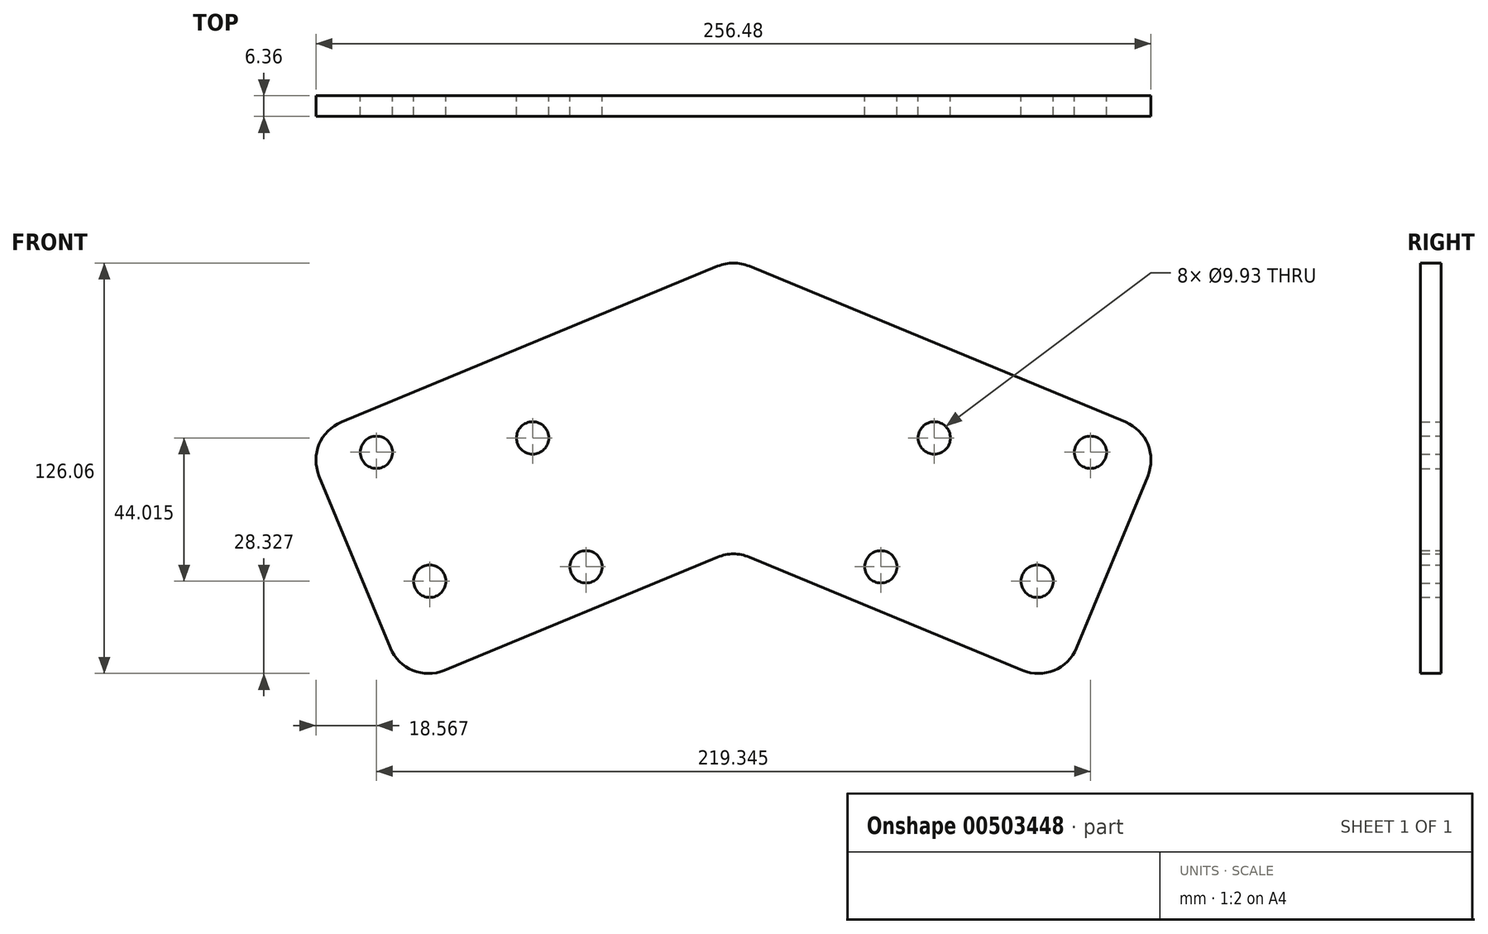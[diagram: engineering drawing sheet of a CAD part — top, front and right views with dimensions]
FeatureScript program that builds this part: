
annotation { "Feature Type Name" : "Feature", "Feature Type Description" : "" }
export const myFeature = defineFeature(function(context is Context, id is Id, definition is map)
    precondition{}
    {
        {
            var Q0;
            Q0=qCreatedBy(makeId("Front.planeOp"),FACE);
            var sketch = newSketch(context, id + "F0", { "sketchPlane" : qUnion([Q0])});
            skLineSegment(sketch, "E0", {"start": v(0, 0) * mm, "end": v(-100.54, -41.65) * mm});
            skLineSegment(sketch, "E1", {"start": v(0, 0) * mm, "end": v(0, 89.35) * mm});
            skLineSegment(sketch, "E2", {"start": v(-100.54, -41.65) * mm, "end": v(-132.13, 34.62) * mm});
            skLineSegment(sketch, "E3", {"start": v(-132.13, 34.62) * mm, "end": v(0, 89.35) * mm});
            skPoint(sketch, "E4", {"position": v(-15.88, 98.24) * mm});
            skPoint(sketch, "E5", {"position": v(-15.88, -22.04) * mm});
            skLineSegment(sketch, "E6.MirrorCS", {"start": v(0, 0) * mm, "end": v(100.54, -41.65) * mm});
            skPoint(sketch, "E7.MirrorP", {"position": v(15.88, -22.04) * mm});
            skLineSegment(sketch, "E8.MirrorCS", {"start": v(100.54, -41.65) * mm, "end": v(132.13, 34.62) * mm});
            skLineSegment(sketch, "E9.MirrorCS", {"start": v(132.13, 34.62) * mm, "end": v(0, 89.35) * mm});
            skPoint(sketch, "E10.MirrorP", {"position": v(15.88, 98.24) * mm});
            skLineSegment(sketch, "E11", {"start": v(-15.88, -22.04) * mm, "end": v(-45.04, 48.36) * mm, "construction": true});
            skLineSegment(sketch, "E12", {"start": v(-15.88, 98.24) * mm, "end": v(13.29, 27.84) * mm, "construction": true});
            skCircle(sketch, "E13", {"center": v(-93.27, -9.42) * mm, "radius": 4.97 * mm});
            skLineSegment(sketch, "E14", {"start": v(-93.27, -9.42) * mm, "end": v(-114.53, 41.91) * mm, "construction": true});
            skCircle(sketch, "E15", {"center": v(-109.67, 30.18) * mm, "radius": 4.97 * mm});
            skCircle(sketch, "E16.MirrorC", {"center": v(93.27, -9.42) * mm, "radius": 4.97 * mm});
            skCircle(sketch, "E17.MirrorC", {"center": v(109.67, 30.18) * mm, "radius": 4.97 * mm});
            skCircle(sketch, "E18", {"center": v(-61.68, 34.6) * mm, "radius": 4.97 * mm});
            skLineSegment(sketch, "E19", {"start": v(-61.68, 34.6) * mm, "end": v(-40.42, -16.74) * mm});
            skCircle(sketch, "E20", {"center": v(-45.28, -5) * mm, "radius": 4.97 * mm});
            skCircle(sketch, "E21.MirrorC", {"center": v(45.28, -5) * mm, "radius": 4.97 * mm});
            skCircle(sketch, "E22.MirrorC", {"center": v(61.68, 34.6) * mm, "radius": 4.97 * mm});
            skPoint(sketch, "E23", {"position": v(-103.9, 16.24) * mm});
            skSolve(sketch);
        }
        {
            var Q0;
            Q0=qSketchRegion(id+"F0",true);
            extrude(context, id + "F1", {"entities" : qUnion([Q0]), "depth" : 6.35 * mm, "offsetDistance" : 25.4 * mm, "symmetric" : true});
        }
        {
            var Q0;
            Q0=makeQuery(id+"F1.opExtrude","SWEPT_EDGE",EDGE,{"disambiguationData":[OSD([sQuery(id+"F0.wireOp",EDGE,"E2"),sQuery(id+"F0.wireOp",EDGE,"E3")])]});
            var Q1;
            Q1=makeQuery(id+"F1.opExtrude","SWEPT_EDGE",EDGE,{"disambiguationData":[OSD([sQuery(id+"F0.wireOp",EDGE,"E3"),sQuery(id+"F0.wireOp",EDGE,"E1"),sQuery(id+"F0.wireOp",EDGE,"E9.MirrorCS")])]});
            var Q2;
            Q2=makeQuery(id+"F1.opExtrude","SWEPT_EDGE",EDGE,{"disambiguationData":[OSD([sQuery(id+"F0.wireOp",EDGE,"E0"),sQuery(id+"F0.wireOp",EDGE,"E6.MirrorCS"),sQuery(id+"F0.wireOp",EDGE,"E1")])]});
            var Q3;
            Q3=makeQuery(id+"F1.opExtrude","SWEPT_EDGE",EDGE,{"disambiguationData":[OSD([sQuery(id+"F0.wireOp",EDGE,"E6.MirrorCS"),sQuery(id+"F0.wireOp",EDGE,"E8.MirrorCS")])]});
            var Q4;
            Q4=makeQuery(id+"F1.opExtrude","SWEPT_EDGE",EDGE,{"disambiguationData":[OSD([sQuery(id+"F0.wireOp",EDGE,"E8.MirrorCS"),sQuery(id+"F0.wireOp",EDGE,"E9.MirrorCS")])]});
            var Q5;
            Q5=makeQuery(id+"F1.opExtrude","SWEPT_EDGE",EDGE,{"disambiguationData":[OSD([sQuery(id+"F0.wireOp",EDGE,"E0"),sQuery(id+"F0.wireOp",EDGE,"E2")])]});
            fillet(context, id + "F2", {"entities" : qUnion([Q0, Q1, Q2, Q3, Q4, Q5]), "radius" : 12.7 * mm, "tangentPropagation" : true, "defaultsChanged" : false, "vertexSettings" : [], "allowEdgeOverflow" : false});
        }
    });
